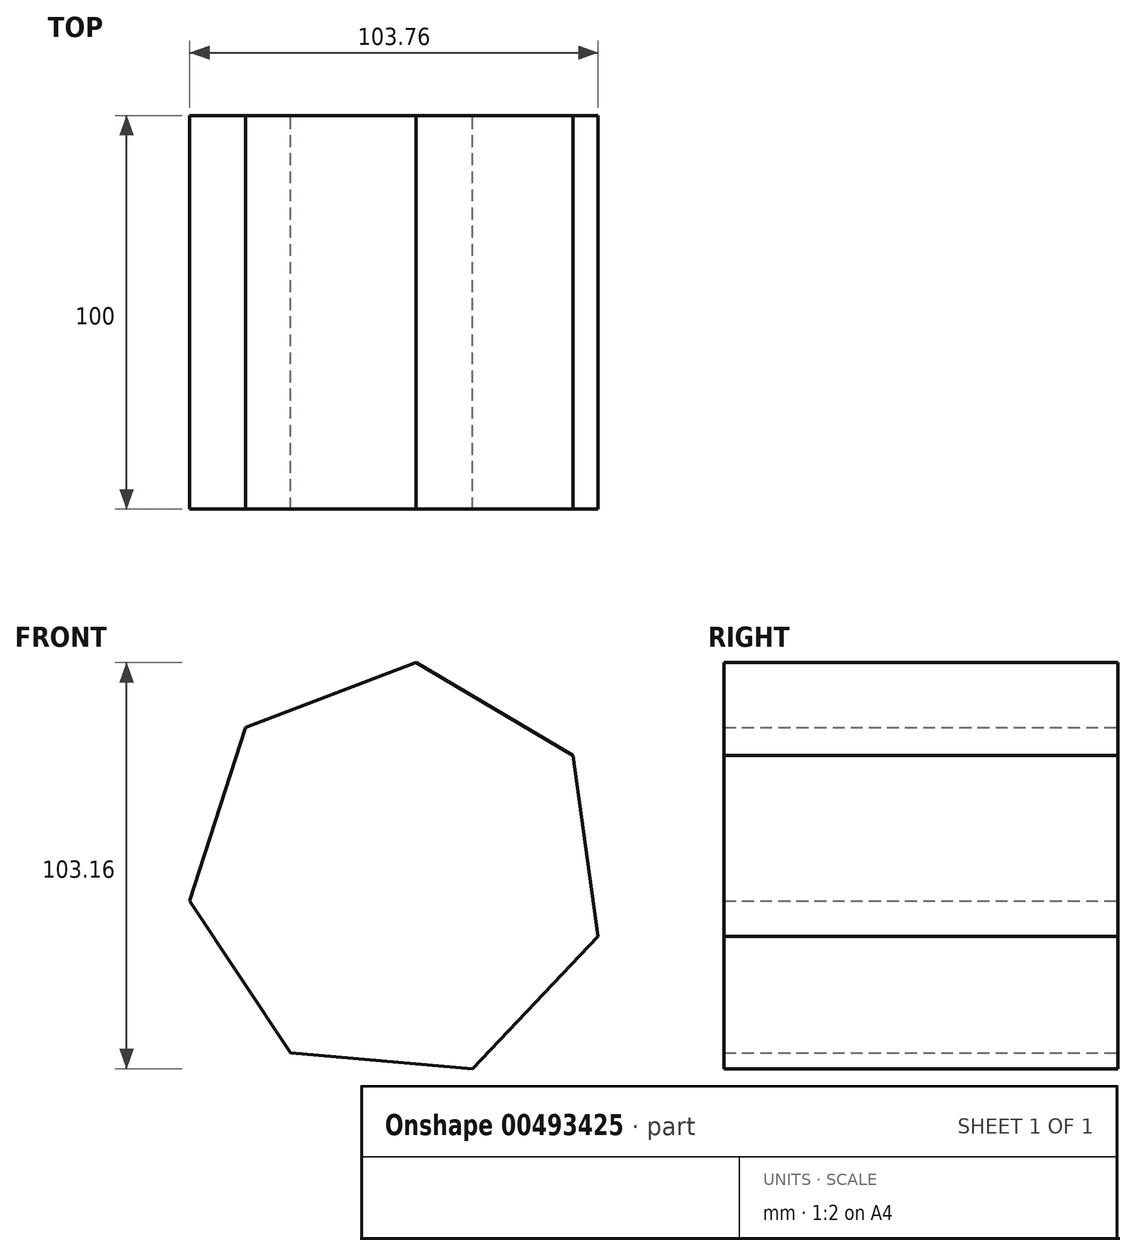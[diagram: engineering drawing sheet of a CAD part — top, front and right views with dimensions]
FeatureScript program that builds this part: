
annotation { "Feature Type Name" : "Feature", "Feature Type Description" : "" }
export const myFeature = defineFeature(function(context is Context, id is Id, definition is map)
    precondition{}
    {
        {
            var Q0;
            Q0=qCreatedBy(makeId("Front.planeOp"),FACE);
            var sketch = newSketch(context, id + "F0", { "sketchPlane" : qUnion([Q0])});
            skCircle(sketch, "E0.cCircle", {"center": v(0, 0) * mm, "radius": 53.41 * mm, "construction": true});
            skLineSegment(sketch, "E0.0", {"start": v(4.6, 53.22) * mm, "end": v(44.47, 29.6) * mm});
            skLineSegment(sketch, "E0.1", {"start": v(44.47, 29.6) * mm, "end": v(50.86, -16.32) * mm});
            skLineSegment(sketch, "E0.2", {"start": v(50.86, -16.32) * mm, "end": v(18.95, -49.94) * mm});
            skLineSegment(sketch, "E0.3", {"start": v(18.95, -49.94) * mm, "end": v(-27.23, -45.96) * mm});
            skLineSegment(sketch, "E0.4", {"start": v(-27.23, -45.96) * mm, "end": v(-52.9, -7.37) * mm});
            skLineSegment(sketch, "E0.5", {"start": v(-52.9, -7.37) * mm, "end": v(-38.74, 36.77) * mm});
            skLineSegment(sketch, "E0.6", {"start": v(-38.74, 36.77) * mm, "end": v(4.6, 53.22) * mm});
            skSolve(sketch);
        }
        {
            var Q0;
            Q0=makeQuery(id+"F0.imprint","IMPRINT",FACE,{"disambiguationData":[TD([[makeQuery(id+"F0.imprint","IMPRINT",EDGE,{"derivedFrom":sQuery(id+"F0.wireOp",EDGE,"E0.0")}),-1.0]])]});
            extrude(context, id + "F1", {"entities" : qUnion([Q0]), "depth" : 100 * mm});
        }
    });
